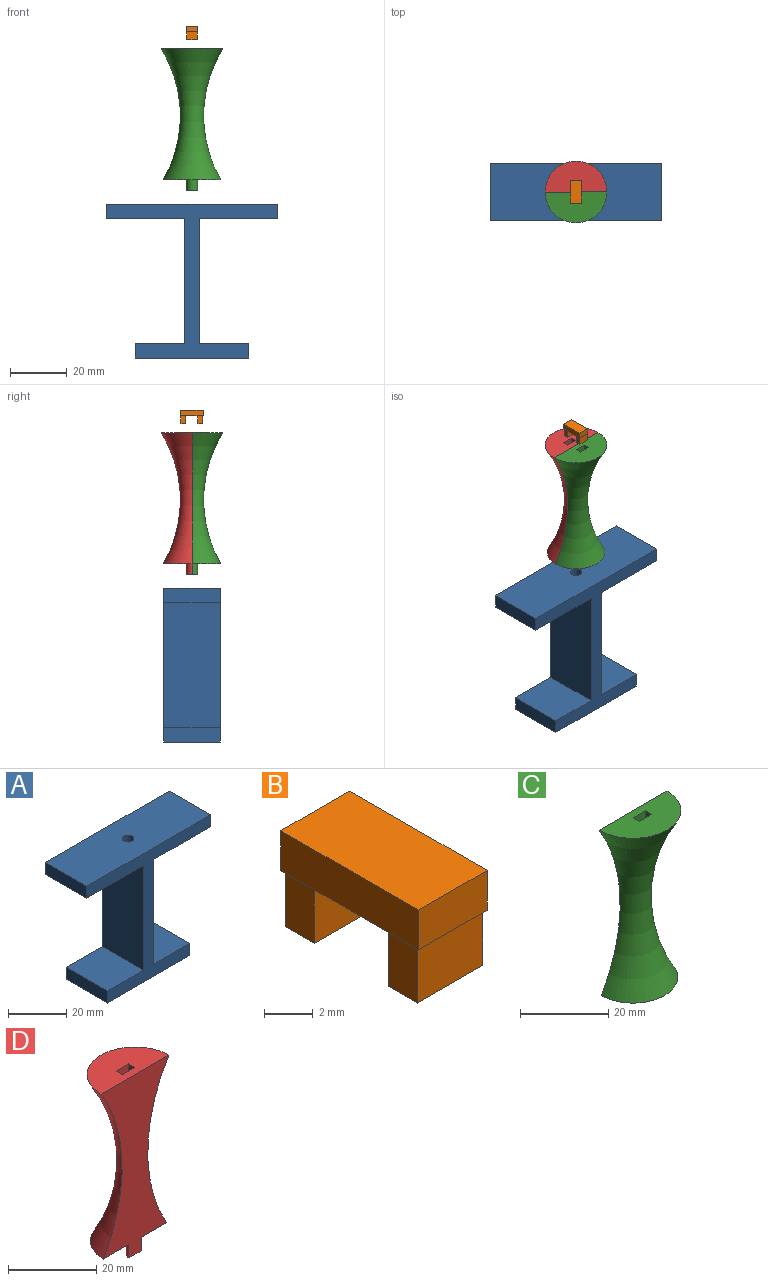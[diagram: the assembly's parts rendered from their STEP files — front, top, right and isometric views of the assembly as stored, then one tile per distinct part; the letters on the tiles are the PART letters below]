
ASSEMBLY  parts=4 mates=3
PART A: 16 faces, bbox 60x20x54 mm
  f0: plane 20x17.5mm, normal (0,0,1), area 350mm2, adj f1,f11,f12,f13
  f1: plane 20x5mm, normal (-1,0,0), area 100mm2, adj f0,f2,f12,f13
  f2: plane 40x20mm, normal (0,0,-1), area 800mm2, adj f1,f3,f12,f13
  f3: plane 20x5mm, normal (1,0,0), area 100mm2, adj f2,f4,f12,f13
  f4: plane 20x17.5mm, normal (0,0,1), area 350mm2, adj f3,f5,f12,f13
  f5: plane 44x20mm, normal (1,0,0), area 880mm2, adj f4,f6,f12,f13
  f6: plane 27.5x20mm, normal (0,0,-1), area 550mm2, adj f5,f7,f12,f13
  f7: plane 20x5mm, normal (1,0,0), area 100mm2, adj f6,f8,f12,f13
  f8: plane 60x20mm, normal (0,0,1), area 1187.4mm2, adj f7,f9,f12,f13,f14
  f9: plane 20x5mm, normal (-1,0,0), area 100mm2, adj f8,f10,f12,f13
  f10: plane 27.5x20mm, normal (0,0,-1), area 550mm2, adj f9,f11,f12,f13
  f11: plane 44x20mm, normal (-1,0,0), area 880mm2, adj f0,f10,f12,f13
  f12: plane 60x54mm, normal (0,-1,0), area 720mm2, adj f0,f1,f2,f3,f4,f5,f6,f7
  f13: plane 60x54mm, normal (0,1,0), area 720mm2, adj f0,f1,f2,f3,f4,f5,f6,f7
  f14: cylinder r=2mm len=4mm, axis (0,0,1), area 50.3mm2, adj f8,f15
  f15: plane 4x4mm, normal (0,0,1), area 12.6mm2, adj f14
PART B: 16 faces, bbox 4x8x4.8 mm
  f0: plane 8x4mm, normal (0,0,-1), area 19.1mm2, adj f1,f2,f3,f4,f6,f7,f8,f9
  f1: plane 8x2mm, normal (1,0,0), area 16mm2, adj f0,f2,f4,f5
  f2: plane 4x2mm, normal (0,1,0), area 8mm2, adj f0,f1,f3,f5
  f3: plane 8x2mm, normal (-1,0,0), area 16mm2, adj f0,f2,f4,f5
  f4: plane 4x2mm, normal (0,-1,0), area 8mm2, adj f0,f1,f3,f5
  f5: plane 8x4mm, normal (0,0,1), area 32mm2, adj f1,f2,f3,f4
  f6: plane 2.8x1.7mm, normal (-1,0,0), area 4.8mm2, adj f0,f7,f9,f10
  f7: plane 3.8x2.8mm, normal (0,1,0), area 10.6mm2, adj f0,f6,f8,f10
  f8: plane 2.8x1.7mm, normal (1,0,0), area 4.8mm2, adj f0,f7,f9,f10
  f9: plane 3.8x2.8mm, normal (0,-1,0), area 10.6mm2, adj f0,f6,f8,f10
  f10: plane 3.8x1.7mm, normal (0,0,-1), area 6.5mm2, adj f6,f7,f8,f9
  f11: plane 2.8x1.7mm, normal (1,0,0), area 4.8mm2, adj f0,f12,f14,f15
  f12: plane 3.8x2.8mm, normal (0,-1,0), area 10.6mm2, adj f0,f11,f13,f15
  f13: plane 2.8x1.7mm, normal (-1,0,0), area 4.8mm2, adj f0,f12,f14,f15
  f14: plane 3.8x2.8mm, normal (0,1,0), area 10.6mm2, adj f0,f11,f13,f15
  f15: plane 3.8x1.7mm, normal (0,0,-1), area 6.5mm2, adj f11,f12,f13,f14
PART C: 11 faces, bbox 37x18.5x63.7 mm
  f0: torus R=48.98mm, axis (0,0,-1), area 952.3mm2, adj f1,f2,f5
  f1: plane 20.23x10.12mm, normal (0,0,-1), area 154.8mm2, adj f0,f3,f5
  f2: plane 21.73x10.86mm, normal (0,0,1), area 177.4mm2, adj f0,f5,f6,f7,f8,f9
  f3: cylinder r=1.95mm len=3.9mm, axis (0,0,1), area 23.3mm2, adj f1,f4,f5
  f4: plane 3.9x1.95mm, normal (0,0,-1), area 6mm2, adj f3,f5
  f5: plane 49.96x21.73mm, normal (0,1,0), area 583.9mm2, adj f0,f1,f2,f3,f4
  f6: plane 3x2mm, normal (1,0,0), area 6mm2, adj f2,f7,f9,f10
  f7: plane 4x3mm, normal (0,1,0), area 12mm2, adj f2,f6,f8,f10
  f8: plane 3x2mm, normal (-1,0,0), area 6mm2, adj f2,f7,f9,f10
  f9: plane 4x3mm, normal (0,-1,0), area 12mm2, adj f2,f6,f8,f10
  f10: plane 4x2mm, normal (0,0,1), area 8mm2, adj f6,f7,f8,f9
PART D: 11 faces, bbox 37x18.5x63.7 mm
  f0: plane 49.96x21.73mm, normal (0,-1,0), area 583.9mm2, adj f1,f2,f3,f4,f5
  f1: plane 21.73x10.86mm, normal (0,0,1), area 177.4mm2, adj f0,f5,f6,f7,f8,f9
  f2: plane 3.9x1.95mm, normal (0,0,-1), area 6mm2, adj f0,f3
  f3: cylinder r=1.95mm len=3.9mm, axis (0,0,1), area 23.3mm2, adj f0,f2,f4
  f4: plane 20.23x10.12mm, normal (0,0,-1), area 154.8mm2, adj f0,f3,f5
  f5: torus R=48.98mm, axis (0,0,-1), area 952.3mm2, adj f0,f1,f4
  f6: plane 4x3mm, normal (0,1,0), area 12mm2, adj f1,f7,f9,f10
  f7: plane 3x2mm, normal (-1,0,0), area 6mm2, adj f1,f6,f8,f10
  f8: plane 4x3mm, normal (0,-1,0), area 12mm2, adj f1,f7,f9,f10
  f9: plane 3x2mm, normal (1,0,0), area 6mm2, adj f1,f6,f8,f10
  f10: plane 4x2mm, normal (0,0,1), area 8mm2, adj f6,f7,f8,f9
PLACE A t=(-24.57,-3.99,17.16)mm
PLACE B t=(-74.07,-3.94,15.26)mm
PLACE C t=(-74.07,-3.99,25.78)mm
PLACE D t=(-74.07,-3.99,25.78)mm
MATE slider B.f15 <-> C.f10  axis (0,0,-1) through (-27.07,-6.09,74.26)mm
MATE slider C.f3 <-> A.f14  axis (0,0,1) through (-27.07,-3.99,21.12)mm
MATE fastened C.f5 <-> D.f0  axis (0,1,0) through (-27.07,-3.99,47.79)mm
